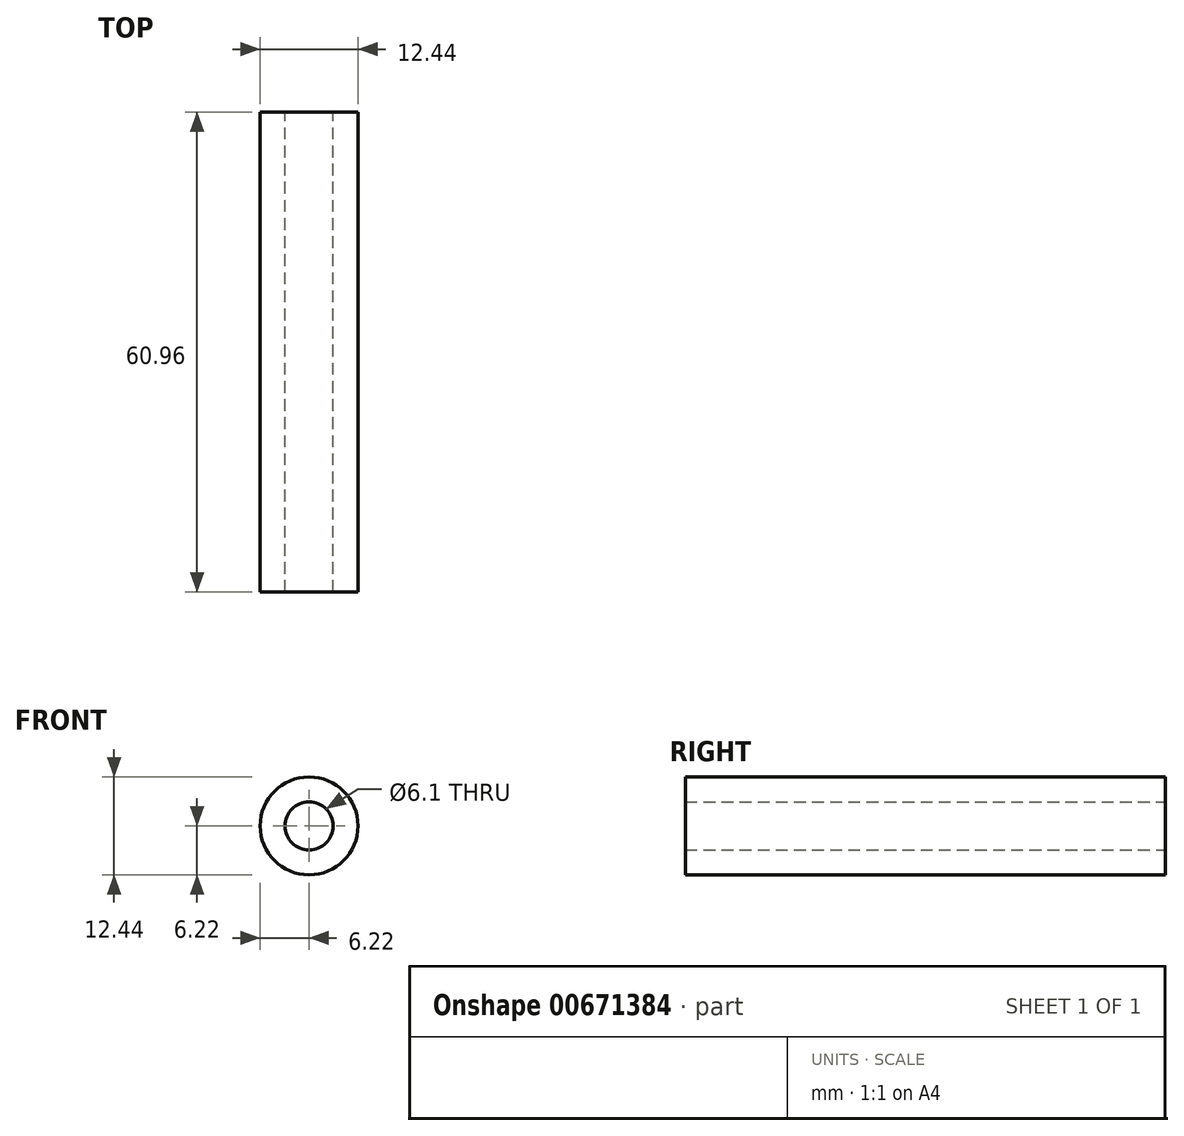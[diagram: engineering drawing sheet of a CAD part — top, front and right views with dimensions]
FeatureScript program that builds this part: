
annotation { "Feature Type Name" : "Feature", "Feature Type Description" : "" }
export const myFeature = defineFeature(function(context is Context, id is Id, definition is map)
    precondition{}
    {
        {
            var Q0;
            Q0=qCreatedBy(makeId("Front.planeOp"),FACE);
            var sketch = newSketch(context, id + "F0", { "sketchPlane" : qUnion([Q0])});
            skCircle(sketch, "E0", {"center": v(0, 0) * mm, "radius": 6.22 * mm});
            skCircle(sketch, "E1", {"center": v(0, 0) * mm, "radius": 3.05 * mm});
            skSolve(sketch);
        }
        {
            var Q0;
            Q0 = qSketchRegion(id + "F0", true);
            extrude(context, id + "F1", {"entities" : qUnion([Q0]), "depth" : 60.96 * mm, "offsetDistance" : 25.4 * mm});
        }
    });
